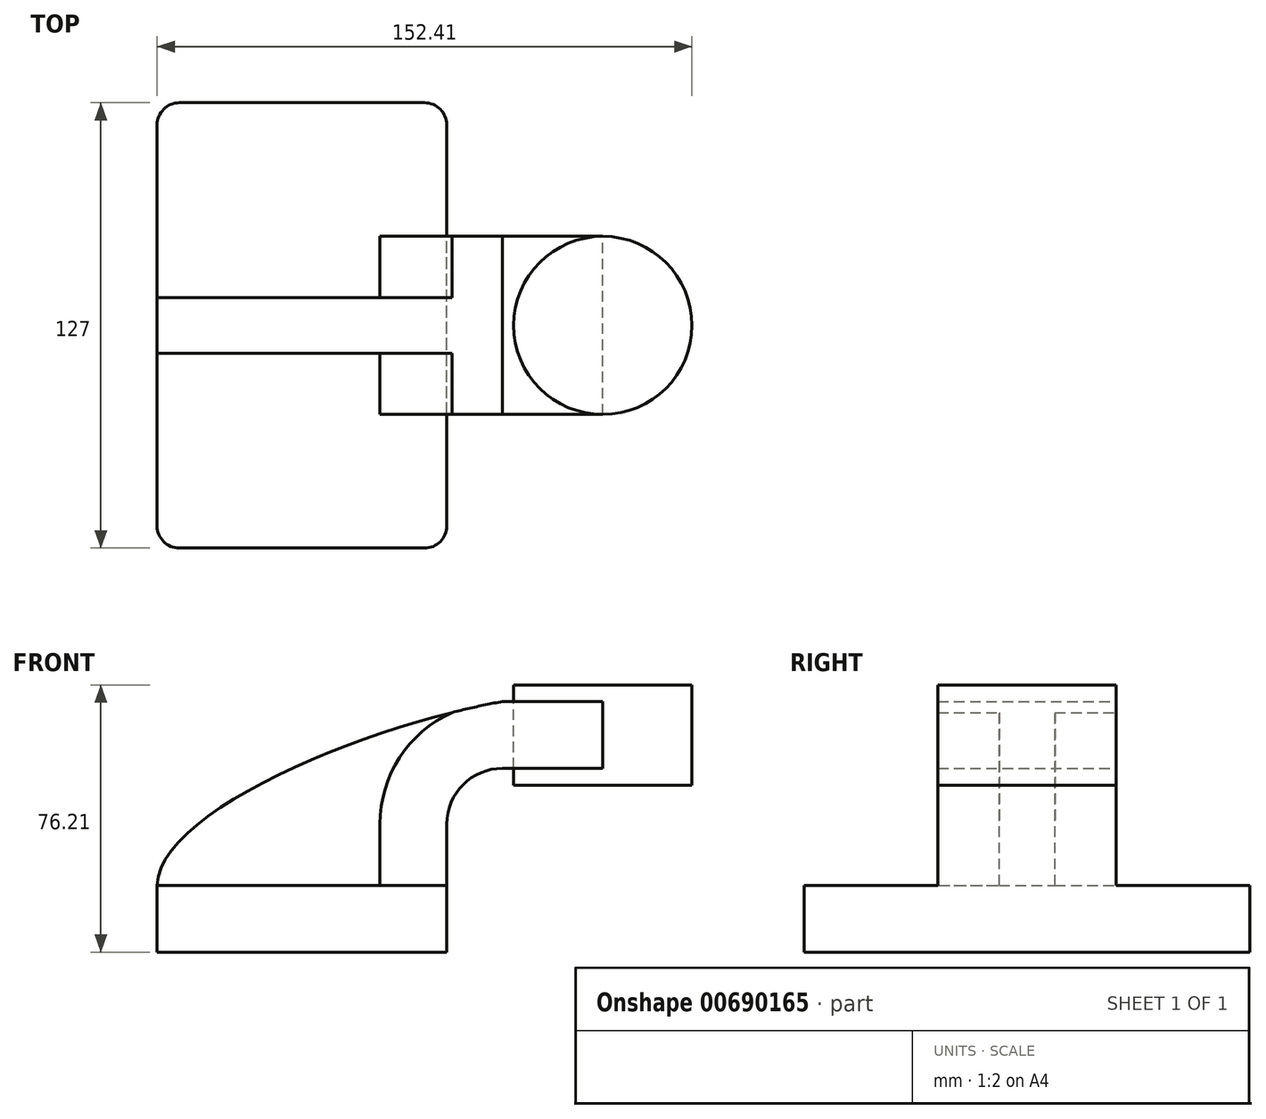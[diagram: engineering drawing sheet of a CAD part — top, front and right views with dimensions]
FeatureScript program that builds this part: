
annotation { "Feature Type Name" : "Feature", "Feature Type Description" : "" }
export const myFeature = defineFeature(function(context is Context, id is Id, definition is map)
    precondition{}
    {
        {
            var Q0;
            Q0=qCreatedBy(makeId("Front.planeOp"),FACE);
            var sketch = newSketch(context, id + "F0", { "sketchPlane" : qUnion([Q0])});
            skLineSegment(sketch, "E0.bottom", {"start": v(-41.28, -9.53) * mm, "end": v(41.28, -9.53) * mm});
            skLineSegment(sketch, "E0.top", {"start": v(-41.28, 9.53) * mm, "end": v(41.28, 9.53) * mm});
            skLineSegment(sketch, "E0.left", {"start": v(-41.28, -9.53) * mm, "end": v(-41.28, 9.53) * mm});
            skLineSegment(sketch, "E0.right", {"start": v(41.28, -9.53) * mm, "end": v(41.28, 9.53) * mm});
            skPoint(sketch, "E0.middle", {"position": v(0, 0) * mm});
            skLineSegment(sketch, "E1.bottom", {"start": v(60.32, 38.1) * mm, "end": v(111.12, 38.1) * mm});
            skLineSegment(sketch, "E1.top", {"start": v(60.32, 66.68) * mm, "end": v(111.12, 66.68) * mm});
            skLineSegment(sketch, "E1.left", {"start": v(60.33, 38.1) * mm, "end": v(60.32, 66.68) * mm});
            skLineSegment(sketch, "E1.right", {"start": v(111.12, 38.1) * mm, "end": v(111.12, 66.68) * mm});
            skPoint(sketch, "E1.middle", {"position": v(85.72, 52.39) * mm});
            skLineSegment(sketch, "E2", {"start": v(41.28, 9.53) * mm, "end": v(41.28, 27) * mm});
            skArc(sketch, "E3", {"start": v(41.28, 27) * mm, "mid": v(45.92, 38.23) * mm, "end": v(57.15, 42.88) * mm});
            skLineSegment(sketch, "E4", {"start": v(57.15, 42.88) * mm, "end": v(85.72, 42.88) * mm});
            skLineSegment(sketch, "E5", {"start": v(85.72, 42.88) * mm, "end": v(85.72, 42.88) * mm});
            skLineSegment(sketch, "E6.0", {"start": v(57.15, 61.93) * mm, "end": v(85.72, 61.93) * mm});
            skArc(sketch, "E6.1", {"start": v(22.23, 27) * mm, "mid": v(32.45, 51.7) * mm, "end": v(57.15, 61.93) * mm});
            skLineSegment(sketch, "E6.2", {"start": v(22.23, 9.53) * mm, "end": v(22.23, 27) * mm});
            skLineSegment(sketch, "E7", {"start": v(85.72, 61.93) * mm, "end": v(85.72, 42.88) * mm});
            skFitSpline(sketch, "E8", {"points": [v(-41.28, 9.53) * mm, v(57.15, 61.93) * mm], "startDerivative": vector(0.78, 63) * mm, "endDerivative": vector(117.72, 20.9) * mm});
            skLineSegment(sketch, "E9", {"start": v(85.72, 66.68) * mm, "end": v(85.72, 38.1) * mm});
            skSolve(sketch);
        }
        {
            var Q0;
            {var subQ0=sQuery(id+"F0.wireOp",EDGE,"E2");Q0=makeQuery(id+"F0.imprint","IMPRINT",FACE,{"disambiguationData":[TD([[makeQuery(id+"F0.imprint","IMPRINT",EDGE,{"derivedFrom":subQ0}),1.0]])]});}
            extrude(context, id + "F1", {"entities" : qUnion([Q0]), "endBound" : BoundingType.SYMMETRIC, "depth" : 50.8 * mm, "offsetDistance" : 25.4 * mm});
        }
        {
            var Q0;
            Q0=makeQuery(id+"F0.imprint","IMPRINT",FACE,{"disambiguationData":[TD([[makeQuery(id+"F0.imprint","IMPRINT",EDGE,{"derivedFrom":sQuery(id+"F0.wireOp",EDGE,"E0.bottom")}),1.0]])]});
            extrude(context, id + "F2", {"entities" : qUnion([Q0]), "operationType" : NewBodyOperationType.ADD, "endBound" : BoundingType.SYMMETRIC, "depth" : 127 * mm, "offsetDistance" : 25.4 * mm});
        }
        {
            var Q0;
            {var subQ0=sQuery(id+"F0.wireOp",EDGE,"E4");var subQ1=sQuery(id+"F0.wireOp",EDGE,"E1.left");var subQ2=makeQuery(id+"F0.imprint","INTERSECT",VERTEX,{"derivedFrom":[subQ1,subQ0]});Q0=makeQuery(id+"F0.imprint","IMPRINT",FACE,{"disambiguationData":[TD([[makeQuery(id+"F0.imprint","IMPRINT",EDGE,{"disambiguationData":[TD([[subQ2,-1.0]])],"derivedFrom":subQ1}),-1.0]])]});}
            extrude(context, id + "F3", {"entities" : qUnion([Q0]), "operationType" : NewBodyOperationType.ADD, "endBound" : BoundingType.SYMMETRIC, "depth" : 50.8 * mm, "offsetDistance" : 25.4 * mm});
        }
        {
            var Q0;
            {var subQ3=sQuery(id+"F0.wireOp",EDGE,"E6.2");Q0=makeQuery(id+"F0.imprint","IMPRINT",FACE,{"disambiguationData":[TD([[makeQuery(id+"F0.imprint","IMPRINT",EDGE,{"derivedFrom":subQ3}),1.0]])]});}
            extrude(context, id + "F4", {"entities" : qUnion([Q0]), "operationType" : NewBodyOperationType.ADD, "endBound" : BoundingType.SYMMETRIC, "depth" : 15.88 * mm, "offsetDistance" : 25.4 * mm});
        }
        {
            var Q0;
            {var subQ4=sQuery(id+"F0.wireOp",EDGE,"E1.right");Q0=makeQuery(id+"F0.imprint","IMPRINT",FACE,{"disambiguationData":[TD([[makeQuery(id+"F0.imprint","IMPRINT",EDGE,{"derivedFrom":subQ4}),1.0]])]});}
            var Q1;
            Q1=sQuery(id+"F0.wireOp",EDGE,"E9");
            revolve(context, id + "F5", {"entities" : qUnion([Q0]), "axis" : qUnion([Q1]), "revolveType" : RevolveType.FULL});
        }
        {
            var Q0;
            Q0=makeQuery(id+"F2.opExtrude","CAP_EDGE",EDGE,{"disambiguationData":[OSD([sQuery(id+"F0.wireOp",EDGE,"E0.right")])],"isStart":false});
            var Q1;
            Q1=makeQuery(id+"F2.opExtrude","CAP_EDGE",EDGE,{"disambiguationData":[OSD([sQuery(id+"F0.wireOp",EDGE,"E0.left")])],"isStart":false});
            var Q2;
            Q2=makeQuery(id+"F2.opExtrude","CAP_EDGE",EDGE,{"disambiguationData":[OSD([sQuery(id+"F0.wireOp",EDGE,"E0.right")])],"isStart":true});
            var Q3;
            Q3=makeQuery(id+"F2.opExtrude","CAP_EDGE",EDGE,{"disambiguationData":[OSD([sQuery(id+"F0.wireOp",EDGE,"E0.left")])],"isStart":true});
            fillet(context, id + "F6", {"entities" : qUnion([Q0, Q1, Q2, Q3]), "radius" : 6.35 * mm, "tangentPropagation" : true, "allowEdgeOverflow" : false});
        }
    });
